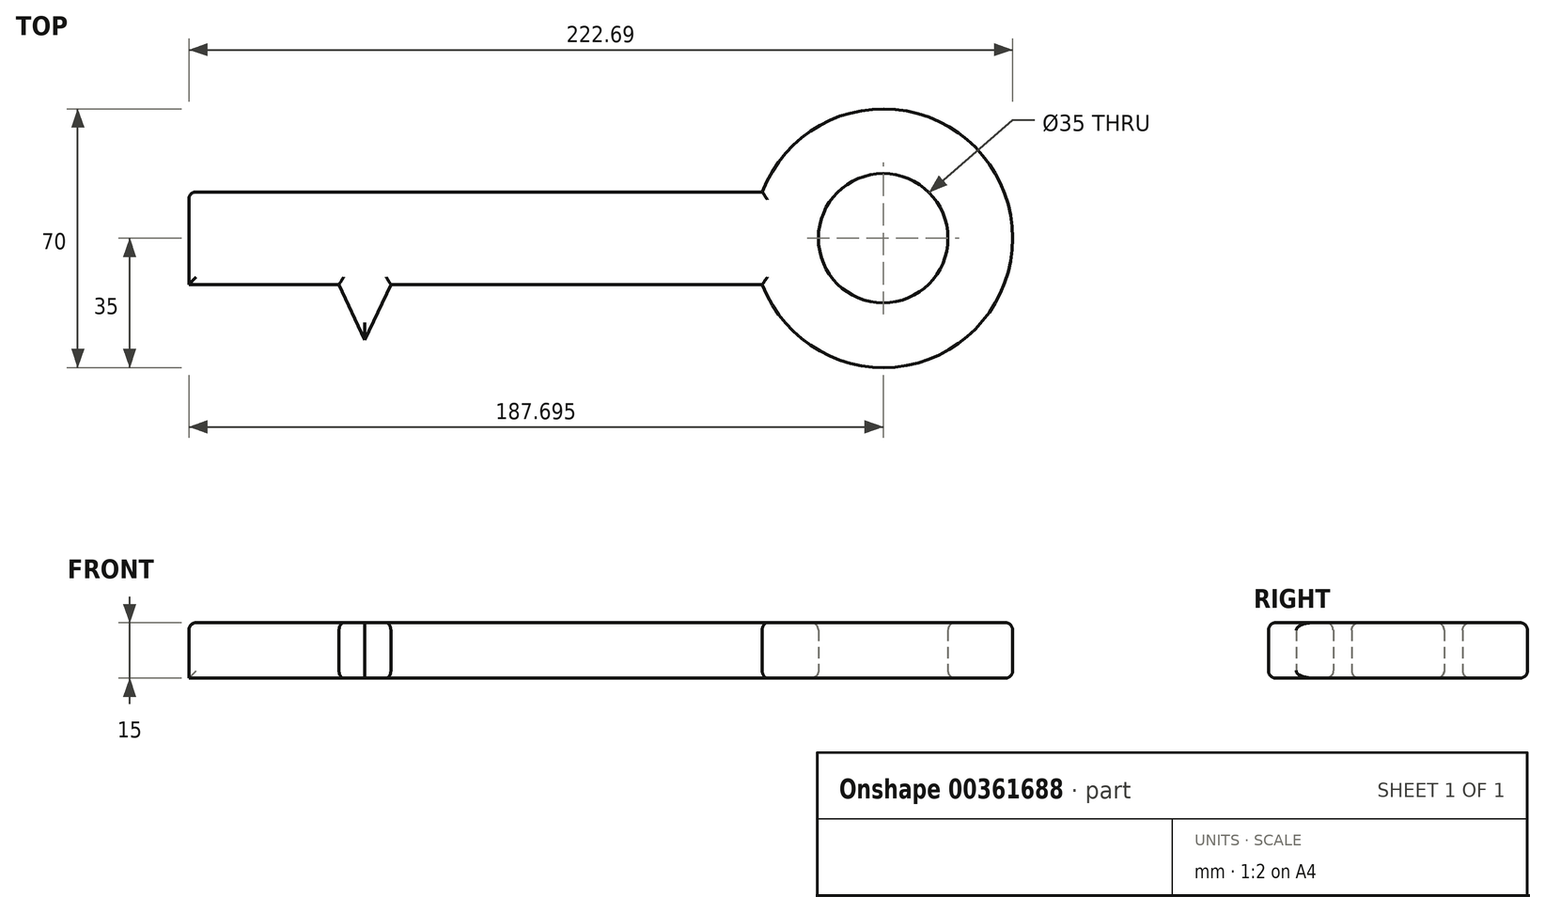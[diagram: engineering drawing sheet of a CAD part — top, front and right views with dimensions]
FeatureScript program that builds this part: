
annotation { "Feature Type Name" : "Feature", "Feature Type Description" : "" }
export const myFeature = defineFeature(function(context is Context, id is Id, definition is map)
    precondition{}
    {
        {
            var Q0;
            Q0=qCreatedBy(makeId("Top.planeOp"),FACE);
            var sketch = newSketch(context, id + "F0", { "sketchPlane" : qUnion([Q0])});
            skLineSegment(sketch, "E0.bottom", {"start": v(27.91, 25) * mm, "end": v(-127.09, 25) * mm});
            skLineSegment(sketch, "E0.top", {"start": v(27.91, 0) * mm, "end": v(-127.09, 0) * mm});
            skLineSegment(sketch, "E0.right", {"start": v(-127.09, 25) * mm, "end": v(-127.09, 0) * mm});
            skLineSegment(sketch, "E1.bottom", {"start": v(-127.09, 0) * mm, "end": v(-117.09, 0) * mm});
            skLineSegment(sketch, "E1.top", {"start": v(-127.09, -30) * mm, "end": v(-117.09, -30) * mm});
            skLineSegment(sketch, "E1.left", {"start": v(-127.09, 0) * mm, "end": v(-127.09, -30) * mm});
            skLineSegment(sketch, "E1.right", {"start": v(-117.09, 0) * mm, "end": v(-117.09, -30) * mm});
            skLineSegment(sketch, "E2.bottom", {"start": v(-104.5, 0) * mm, "end": v(-96.5, 0) * mm});
            skLineSegment(sketch, "E2.top", {"start": v(-104.5, -15.34) * mm, "end": v(-96.5, -15.34) * mm});
            skLineSegment(sketch, "E2.left", {"start": v(-104.5, 0) * mm, "end": v(-104.5, -15.34) * mm});
            skLineSegment(sketch, "E2.right", {"start": v(-96.5, 0) * mm, "end": v(-96.5, -15.34) * mm});
            skLineSegment(sketch, "E3", {"start": v(-86.5, 0) * mm, "end": v(-79.5, -15) * mm});
            skLineSegment(sketch, "E4", {"start": v(-79.5, -15) * mm, "end": v(-72.5, 0) * mm});
            skLineSegment(sketch, "E5", {"start": v(-86.5, 0) * mm, "end": v(-72.5, 0) * mm});
            skArc(sketch, "E6", {"start": v(27.91, 0) * mm, "mid": v(95.6, 12.5) * mm, "end": v(27.91, 25) * mm});
            skCircle(sketch, "E7", {"center": v(60.6, 12.5) * mm, "radius": 17.5 * mm});
            skLineSegment(sketch, "E8", {"start": v(60.6, 12.5) * mm, "end": v(-127.09, 12.5) * mm, "construction": true});
            skSolve(sketch);
        }
        {
            var Q0;
            Q0=makeQuery(id+"F0.imprint","IMPRINT",FACE,{"disambiguationData":[TD([[makeQuery(id+"F0.imprint","IMPRINT",EDGE,{"derivedFrom":sQuery(id+"F0.wireOp",EDGE,"E0.bottom")}),1.0]])]});
            var Q1;
            Q1=makeQuery(id+"F0.imprint","IMPRINT",FACE,{"disambiguationData":[TD([[makeQuery(id+"F0.imprint","IMPRINT",EDGE,{"derivedFrom":sQuery(id+"F0.wireOp",EDGE,"E3")}),1.0]])]});
            var Q2;
            Q2=makeQuery(id+"F0.imprint","IMPRINT",FACE,{"disambiguationData":[TD([[makeQuery(id+"F0.imprint","IMPRINT",EDGE,{"derivedFrom":sQuery(id+"F0.wireOp",EDGE,"E2.bottom")}),-1.0]])]});
            var Q3;
            Q3=makeQuery(id+"F0.imprint","IMPRINT",FACE,{"disambiguationData":[TD([[makeQuery(id+"F0.imprint","IMPRINT",EDGE,{"derivedFrom":sQuery(id+"F0.wireOp",EDGE,"E1.bottom")}),-1.0]])]});
            extrude(context, id + "F1", {"entities" : qUnion([Q0, Q1, Q2, Q3]), "depth" : 15 * mm});
        }
        {
            var Q0;
            Q0=makeQuery(id+"F1.opExtrude","SWEPT_EDGE",EDGE,{"disambiguationData":[OSD([sQuery(id+"F0.wireOp",EDGE,"E0.bottom"),sQuery(id+"F0.wireOp",EDGE,"E0.right")])]});
            var Q1;
            Q1=makeQuery(id+"F1.opExtrude","CAP_EDGE",EDGE,{"disambiguationData":[OSD([sQuery(id+"F0.wireOp",EDGE,"E1.top")])],"isStart":false});
            var Q2;
            Q2=makeQuery(id+"F1.opExtrude","CAP_EDGE",EDGE,{"disambiguationData":[OSD([sQuery(id+"F0.wireOp",EDGE,"E2.top")])],"isStart":false});
            var Q3;
            Q3=makeQuery(id+"F1.opExtrude","CAP_EDGE",EDGE,{"disambiguationData":[OSD([sQuery(id+"F0.wireOp",EDGE,"E3")])],"isStart":false});
            var Q4;
            Q4=makeQuery(id+"F1.opExtrude","CAP_EDGE",EDGE,{"disambiguationData":[OSD([sQuery(id+"F0.wireOp",EDGE,"E4")])],"isStart":false});
            var Q5;
            Q5=makeQuery(id+"F1.opExtrude","CAP_EDGE",EDGE,{"disambiguationData":[OSD([sQuery(id+"F0.wireOp",EDGE,"E6")])],"isStart":false});
            var Q6;
            Q6=makeQuery(id+"F1.opExtrude","CAP_EDGE",EDGE,{"disambiguationData":[OSD([sQuery(id+"F0.wireOp",EDGE,"E6")])],"isStart":true});
            var Q7;
            Q7=makeQuery(id+"F1.opExtrude","CAP_EDGE",EDGE,{"disambiguationData":[OSD([sQuery(id+"F0.wireOp",EDGE,"E7")])],"isStart":true});
            var Q8;
            Q8=makeQuery(id+"F1.opExtrude","CAP_EDGE",EDGE,{"disambiguationData":[OSD([sQuery(id+"F0.wireOp",EDGE,"E7")])],"isStart":false});
            var Q9;
            Q9=makeQuery(id+"F1.opExtrude","CAP_EDGE",EDGE,{"disambiguationData":[OSD([sQuery(id+"F0.wireOp",EDGE,"E0.bottom")])],"isStart":false});
            var Q10;
            Q10=makeQuery(id+"F1.opExtrude","CAP_EDGE",EDGE,{"disambiguationData":[OSD([sQuery(id+"F0.wireOp",EDGE,"E0.bottom")])],"isStart":true});
            var Q11;
            {var subQ0=sQuery(id+"F0.wireOp",EDGE,"E0.top");Q11=makeQuery(id+"F1.opExtrude","CAP_EDGE",EDGE,{"disambiguationData":[OSD([subQ0]),TDD([makeQuery(id+"F0.imprint","IMPRINT",EDGE,{"disambiguationData":[TD([[makeQuery(id+"F0.imprint","INTERSECT",VERTEX,{"derivedFrom":[subQ0,sQuery(id+"F0.wireOp",EDGE,"E6")]}),-1.0]])],"derivedFrom":subQ0})])],"isStart":false});}
            var Q12;
            {var subQ0=sQuery(id+"F0.wireOp",EDGE,"E0.top");Q12=makeQuery(id+"F1.opExtrude","CAP_EDGE",EDGE,{"disambiguationData":[OSD([subQ0]),TDD([makeQuery(id+"F0.imprint","IMPRINT",EDGE,{"disambiguationData":[TD([[makeQuery(id+"F0.imprint","INTERSECT",VERTEX,{"derivedFrom":[subQ0,sQuery(id+"F0.wireOp",EDGE,"E1.bottom"),sQuery(id+"F0.wireOp",EDGE,"E1.right")]}),1.0]])],"derivedFrom":subQ0})])],"isStart":false});}
            var Q13;
            {var subQ0=sQuery(id+"F0.wireOp",EDGE,"E0.top");Q13=makeQuery(id+"F1.opExtrude","CAP_EDGE",EDGE,{"disambiguationData":[OSD([subQ0]),TDD([makeQuery(id+"F0.imprint","IMPRINT",EDGE,{"disambiguationData":[TD([[makeQuery(id+"F0.imprint","INTERSECT",VERTEX,{"derivedFrom":[subQ0,sQuery(id+"F0.wireOp",EDGE,"E2.bottom"),sQuery(id+"F0.wireOp",EDGE,"E2.right")]}),1.0]])],"derivedFrom":subQ0})])],"isStart":false});}
            var Q14;
            Q14=makeQuery(id+"F1.opExtrude","CAP_EDGE",EDGE,{"disambiguationData":[OSD([sQuery(id+"F0.wireOp",EDGE,"E1.right")])],"isStart":false});
            var Q15;
            Q15=makeQuery(id+"F1.opExtrude","CAP_EDGE",EDGE,{"disambiguationData":[OSD([sQuery(id+"F0.wireOp",EDGE,"E0.right"),sQuery(id+"F0.wireOp",EDGE,"E1.left")])],"isStart":false});
            var Q16;
            Q16=makeQuery(id+"F1.opExtrude","CAP_EDGE",EDGE,{"disambiguationData":[OSD([sQuery(id+"F0.wireOp",EDGE,"E2.right")])],"isStart":false});
            var Q17;
            Q17=makeQuery(id+"F1.opExtrude","CAP_EDGE",EDGE,{"disambiguationData":[OSD([sQuery(id+"F0.wireOp",EDGE,"E2.left")])],"isStart":false});
            var Q18;
            {var subQ0=sQuery(id+"F0.wireOp",EDGE,"E0.top");Q18=makeQuery(id+"F1.opExtrude","CAP_EDGE",EDGE,{"disambiguationData":[OSD([subQ0]),TDD([makeQuery(id+"F0.imprint","IMPRINT",EDGE,{"disambiguationData":[TD([[makeQuery(id+"F0.imprint","INTERSECT",VERTEX,{"derivedFrom":[subQ0,sQuery(id+"F0.wireOp",EDGE,"E6")]}),-1.0]])],"derivedFrom":subQ0})])],"isStart":true});}
            var Q19;
            Q19=makeQuery(id+"F1.opExtrude","CAP_EDGE",EDGE,{"disambiguationData":[OSD([sQuery(id+"F0.wireOp",EDGE,"E3")])],"isStart":true});
            var Q20;
            Q20=makeQuery(id+"F1.opExtrude","CAP_EDGE",EDGE,{"disambiguationData":[OSD([sQuery(id+"F0.wireOp",EDGE,"E4")])],"isStart":true});
            var Q21;
            {var subQ0=sQuery(id+"F0.wireOp",EDGE,"E0.top");Q21=makeQuery(id+"F1.opExtrude","CAP_EDGE",EDGE,{"disambiguationData":[OSD([subQ0]),TDD([makeQuery(id+"F0.imprint","IMPRINT",EDGE,{"disambiguationData":[TD([[makeQuery(id+"F0.imprint","INTERSECT",VERTEX,{"derivedFrom":[subQ0,sQuery(id+"F0.wireOp",EDGE,"E2.bottom"),sQuery(id+"F0.wireOp",EDGE,"E2.right")]}),1.0]])],"derivedFrom":subQ0})])],"isStart":true});}
            var Q22;
            Q22=makeQuery(id+"F1.opExtrude","CAP_EDGE",EDGE,{"disambiguationData":[OSD([sQuery(id+"F0.wireOp",EDGE,"E2.right")])],"isStart":true});
            var Q23;
            Q23=makeQuery(id+"F1.opExtrude","CAP_EDGE",EDGE,{"disambiguationData":[OSD([sQuery(id+"F0.wireOp",EDGE,"E2.left")])],"isStart":true});
            var Q24;
            {var subQ0=sQuery(id+"F0.wireOp",EDGE,"E0.top");Q24=makeQuery(id+"F1.opExtrude","CAP_EDGE",EDGE,{"disambiguationData":[OSD([subQ0]),TDD([makeQuery(id+"F0.imprint","IMPRINT",EDGE,{"disambiguationData":[TD([[makeQuery(id+"F0.imprint","INTERSECT",VERTEX,{"derivedFrom":[subQ0,sQuery(id+"F0.wireOp",EDGE,"E1.bottom"),sQuery(id+"F0.wireOp",EDGE,"E1.right")]}),1.0]])],"derivedFrom":subQ0})])],"isStart":true});}
            var Q25;
            Q25=makeQuery(id+"F1.opExtrude","CAP_EDGE",EDGE,{"disambiguationData":[OSD([sQuery(id+"F0.wireOp",EDGE,"E1.right")])],"isStart":true});
            fillet(context, id + "F2", {"entities" : qUnion([Q0, Q1, Q2, Q3, Q4, Q5, Q6, Q7, Q8, Q9, Q10, Q11, Q12, Q13, Q14, Q15, Q16, Q17, Q18, Q19, Q20, Q21, Q22, Q23, Q24, Q25]), "radius" : 2 * mm, "tangentPropagation" : true, "allowEdgeOverflow" : false});
        }
    });
